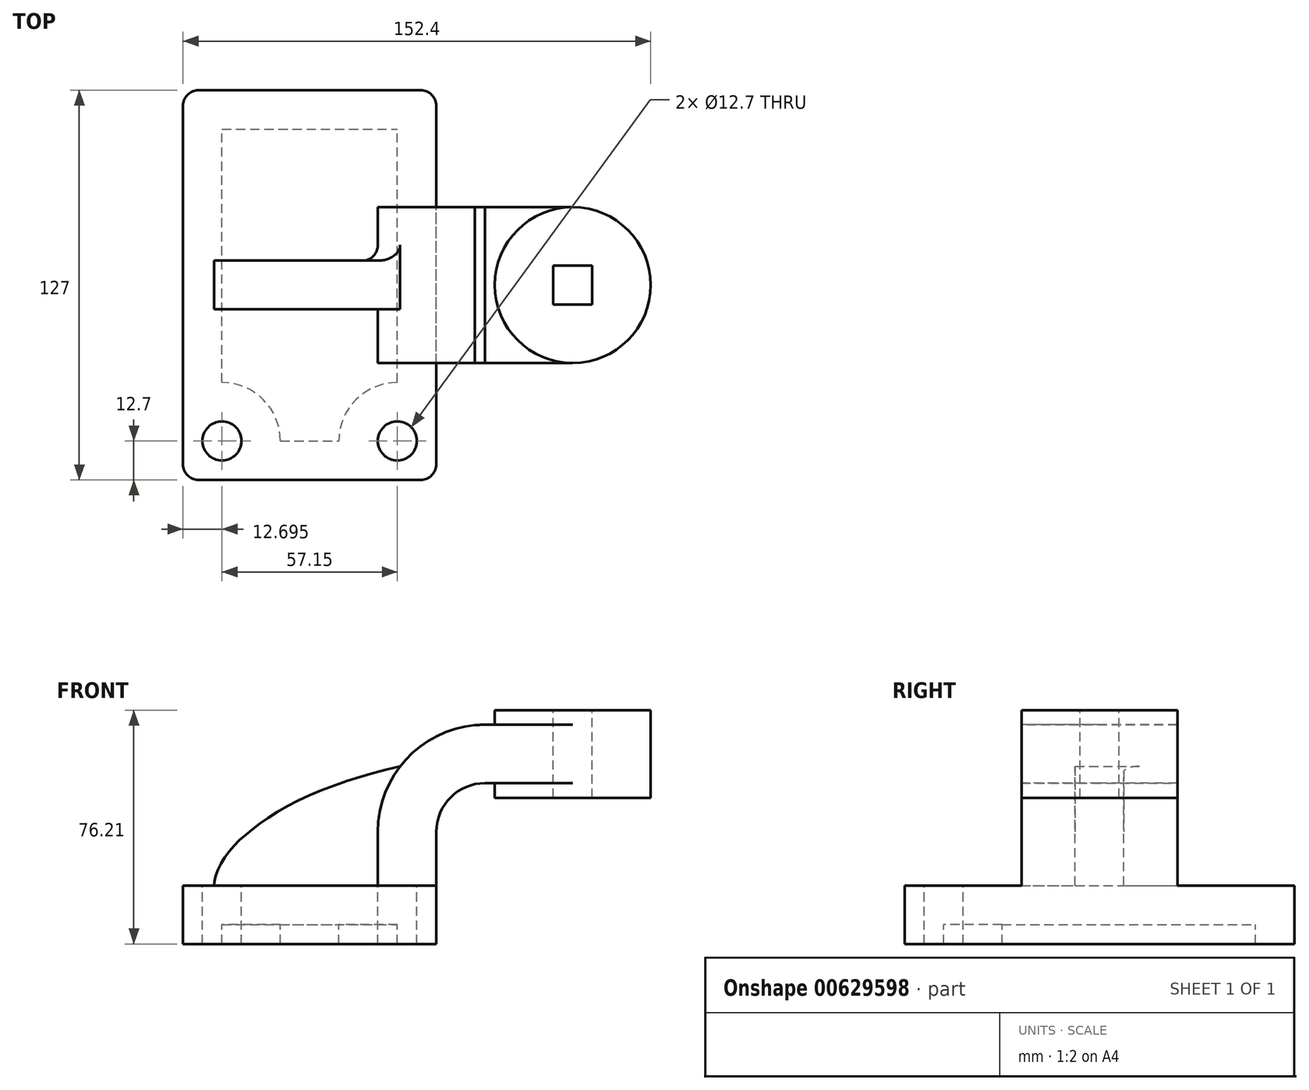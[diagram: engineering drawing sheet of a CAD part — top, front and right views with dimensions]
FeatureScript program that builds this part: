
annotation { "Feature Type Name" : "Feature", "Feature Type Description" : "" }
export const myFeature = defineFeature(function(context is Context, id is Id, definition is map)
    precondition{}
    {
        {
            var Q0;
            Q0=qCreatedBy(makeId("Front.planeOp"),FACE);
            var sketch = newSketch(context, id + "F0", { "sketchPlane" : qUnion([Q0])});
            skLineSegment(sketch, "E0.rect.bottom", {"start": v(-41.28, 9.52) * mm, "end": v(41.28, 9.52) * mm});
            skLineSegment(sketch, "E0.rect.top", {"start": v(-41.28, -9.52) * mm, "end": v(41.28, -9.52) * mm});
            skLineSegment(sketch, "E0.rect.left", {"start": v(-41.28, 9.52) * mm, "end": v(-41.28, -9.52) * mm});
            skLineSegment(sketch, "E0.rect.right", {"start": v(41.28, 9.52) * mm, "end": v(41.28, -9.52) * mm});
            skPoint(sketch, "E0.rect.middle", {"position": v(0, 0) * mm});
            skLineSegment(sketch, "E1", {"start": v(41.28, 9.52) * mm, "end": v(41.28, 27) * mm});
            skArc(sketch, "E2", {"start": v(41.28, 27) * mm, "mid": v(45.92, 38.23) * mm, "end": v(57.15, 42.88) * mm});
            skLineSegment(sketch, "E3", {"start": v(57.15, 42.88) * mm, "end": v(85.72, 42.88) * mm});
            skLineSegment(sketch, "E4.rect.bottom", {"start": v(60.32, 38.1) * mm, "end": v(111.12, 38.1) * mm});
            skLineSegment(sketch, "E4.rect.top", {"start": v(60.32, 66.68) * mm, "end": v(111.12, 66.68) * mm});
            skLineSegment(sketch, "E4.rect.left", {"start": v(60.32, 38.1) * mm, "end": v(60.32, 66.68) * mm});
            skLineSegment(sketch, "E4.rect.right", {"start": v(111.13, 38.1) * mm, "end": v(111.12, 66.68) * mm});
            skPoint(sketch, "E4.rect.middle", {"position": v(85.72, 52.39) * mm});
            skLineSegment(sketch, "E5.0", {"start": v(57.15, 61.93) * mm, "end": v(85.72, 61.93) * mm});
            skArc(sketch, "E5.1", {"start": v(22.23, 27) * mm, "mid": v(32.45, 51.7) * mm, "end": v(57.15, 61.93) * mm});
            skLineSegment(sketch, "E5.2", {"start": v(22.23, 9.52) * mm, "end": v(22.23, 27) * mm});
            skLineSegment(sketch, "E6", {"start": v(85.72, 38.1) * mm, "end": v(85.72, 66.68) * mm});
            skFitSpline(sketch, "E7", {"points": [v(-41.28, 9.53) * mm, v(57.15, 61.93) * mm], "startDerivative": vector(5.2, 92.34) * mm, "endDerivative": vector(120.92, 4.22) * mm});
            skFitSpline(sketch, "E8.0", {"points": [v(-31.13, 8.95) * mm, v(-31.07, 10.12) * mm, v(-30.68, 12.4) * mm, v(-29.3, 15.91) * mm, v(-27.01, 19.59) * mm, v(-23.75, 23.37) * mm, v(-19.56, 27.14) * mm, v(-12.83, 32.04) * mm, v(-2.55, 37.73) * mm, v(11.83, 43.44) * mm, v(27.3, 47.83) * mm, v(42.94, 50.73) * mm, v(52.85, 51.6) * mm, v(57.5, 51.77) * mm]});
            skLineSegment(sketch, "E9.0", {"start": v(-21.14, 19.69) * mm, "end": v(9.52, 19.69) * mm});
            skLineSegment(sketch, "E10.0", {"start": v(12.06, 22.23) * mm, "end": v(12.06, 27) * mm});
            skArc(sketch, "E11.0", {"start": v(12.07, 27) * mm, "mid": v(12.52, 33.38) * mm, "end": v(13.87, 39.62) * mm});
            skArc(sketch, "E12.filletArc", {"start": v(-22.9, 24.05) * mm, "mid": v(-23.5, 21.27) * mm, "end": v(-21.14, 19.69) * mm});
            skArc(sketch, "E13.filletArc", {"start": v(9.52, 19.69) * mm, "mid": v(11.32, 20.43) * mm, "end": v(12.06, 22.23) * mm});
            skArc(sketch, "E14.filletArc", {"start": v(13.87, 39.62) * mm, "mid": v(13.18, 42.18) * mm, "end": v(10.6, 42.73) * mm});
            skSolve(sketch);
        }
        {
            var Q0;
            Q0=makeQuery(id+"F0.imprint","IMPRINT",FACE,{"disambiguationData":[TD([[makeQuery(id+"F0.imprint","IMPRINT",EDGE,{"derivedFrom":sQuery(id+"F0.wireOp",EDGE,"E0.rect.top")}),1.0]])]});
            extrude(context, id + "F1", {"entities" : qUnion([Q0]), "endBound" : BoundingType.SYMMETRIC, "depth" : 127 * mm});
        }
        {
            var Q0;
            {var subQ9=sQuery(id+"F0.wireOp",EDGE,"E1");Q0=makeQuery(id+"F0.imprint","IMPRINT",FACE,{"disambiguationData":[TD([[makeQuery(id+"F0.imprint","IMPRINT",EDGE,{"derivedFrom":subQ9}),1.0]])]});}
            var Q1;
            {var subQ0=sQuery(id+"F0.wireOp",EDGE,"E6");var subQ1=sQuery(id+"F0.wireOp",EDGE,"E3");var subQ2=makeQuery(id+"F0.imprint","INTERSECT",VERTEX,{"derivedFrom":[subQ1,subQ0]});Q1=makeQuery(id+"F0.imprint","IMPRINT",FACE,{"disambiguationData":[TD([[makeQuery(id+"F0.imprint","IMPRINT",EDGE,{"disambiguationData":[TD([[subQ2,1.0]])],"derivedFrom":subQ1}),1.0]])]});}
            extrude(context, id + "F2", {"entities" : qUnion([Q0, Q1]), "operationType" : NewBodyOperationType.ADD, "endBound" : BoundingType.SYMMETRIC, "depth" : 50.8 * mm});
        }
        {
            var Q0;
            {var subQ3=sQuery(id+"F0.wireOp",EDGE,"E5.2");Q0=makeQuery(id+"F0.imprint","IMPRINT",FACE,{"disambiguationData":[TD([[makeQuery(id+"F0.imprint","IMPRINT",EDGE,{"derivedFrom":subQ3}),1.0]])]});}
            extrude(context, id + "F3", {"entities" : qUnion([Q0]), "operationType" : NewBodyOperationType.ADD, "endBound" : BoundingType.SYMMETRIC, "depth" : 15.88 * mm});
        }
        {
            var Q0;
            {var subQ5=sQuery(id+"F0.wireOp",EDGE,"E4.rect.right");Q0=makeQuery(id+"F0.imprint","IMPRINT",FACE,{"disambiguationData":[TD([[makeQuery(id+"F0.imprint","IMPRINT",EDGE,{"derivedFrom":subQ5}),1.0]])]});}
            var Q1;
            Q1=sQuery(id+"F0.wireOp",EDGE,"E6");
            revolve(context, id + "F4", {"operationType" : NewBodyOperationType.ADD, "entities" : qUnion([Q0]), "axis" : qUnion([Q1]), "revolveType" : RevolveType.FULL});
        }
        {
            var Q0;
            Q0=makeQuery(id+"F1.opExtrude","CAP_EDGE",EDGE,{"disambiguationData":[OSD([sQuery(id+"F0.wireOp",EDGE,"E0.rect.right")])],"isStart":false});
            var Q1;
            Q1=makeQuery(id+"F1.opExtrude","CAP_EDGE",EDGE,{"disambiguationData":[OSD([sQuery(id+"F0.wireOp",EDGE,"E0.rect.left")])],"isStart":false});
            var Q2;
            Q2=makeQuery(id+"F1.opExtrude","CAP_EDGE",EDGE,{"disambiguationData":[OSD([sQuery(id+"F0.wireOp",EDGE,"E0.rect.right")])],"isStart":true});
            var Q3;
            Q3=makeQuery(id+"F1.opExtrude","CAP_EDGE",EDGE,{"disambiguationData":[OSD([sQuery(id+"F0.wireOp",EDGE,"E0.rect.left")])],"isStart":true});
            fillet(context, id + "F5", {"entities" : qUnion([Q0, Q1, Q2, Q3]), "radius" : 5.08 * mm, "tangentPropagation" : true, "allowEdgeOverflow" : false});
        }
        {
            var Q0;
            {var subQ4=sQuery(id+"F0.wireOp",EDGE,"E0.rect.bottom");var subQ5=sQuery(id+"F0.wireOp",EDGE,"E0.rect.right");var subQ6=sQuery(id+"F0.wireOp",EDGE,"E0.rect.left");Q0=makeQuery(id+"F3.boolean.opBoolean","SPLIT",FACE,{"disambiguationData":[TD([makeQuery(id+"F1.opExtrude","CAP_FACE",FACE,{"disambiguationData":[OSD([subQ4,sQuery(id+"F0.wireOp",EDGE,"E0.rect.top"),subQ6,subQ5])],"isStart":false})])],"derivedFrom":makeQuery(id+"F1.opExtrude","SWEPT_FACE",FACE,{"disambiguationData":[OSD([subQ4])]})});}
            var sketch = newSketch(context, id + "F6", { "sketchPlane" : qUnion([Q0])});
            skCircle(sketch, "E15", {"center": v(-28.58, -50.8) * mm, "radius": 6.35 * mm});
            skCircle(sketch, "E16", {"center": v(28.58, -50.8) * mm, "radius": 6.35 * mm});
            skSolve(sketch);
        }
        {
            var Q0;
            Q0=makeQuery(id+"F6.imprint","IMPRINT",FACE,{"disambiguationData":[TD([[makeQuery(id+"F6.imprint","IMPRINT",EDGE,{"derivedFrom":sQuery(id+"F6.wireOp",EDGE,"E15")}),1.0]])]});
            var Q1;
            Q1=makeQuery(id+"F6.imprint","IMPRINT",FACE,{"disambiguationData":[TD([[makeQuery(id+"F6.imprint","IMPRINT",EDGE,{"derivedFrom":sQuery(id+"F6.wireOp",EDGE,"E16")}),1.0]])]});
            var Q2;
            Q2=sQuery(id+"F6.wireOp",EDGE,"E15");
            var Q3;
            Q3=sQuery(id+"F6.wireOp",EDGE,"E16");
            extrude(context, id + "F7", {"entities" : qUnion([Q0, Q1]), "operationType" : NewBodyOperationType.REMOVE, "surfaceEntities" : qUnion([Q2, Q3]), "endBound" : BoundingType.THROUGH_ALL, "oppositeDirection" : true, "depth" : 25.4 * mm, "offsetDistance" : 25.4 * mm});
        }
        {
            var Q0;
            Q0=makeQuery(id+"F4.opRevolve","SWEPT_FACE",FACE,{"disambiguationData":[OSD([sQuery(id+"F0.wireOp",EDGE,"E4.rect.top")])]});
            var sketch = newSketch(context, id + "F8", { "sketchPlane" : qUnion([Q0])});
            skLineSegment(sketch, "E17.bottom", {"start": v(92.08, 6.35) * mm, "end": v(79.38, 6.35) * mm});
            skLineSegment(sketch, "E17.top", {"start": v(92.08, -6.35) * mm, "end": v(79.38, -6.35) * mm});
            skLineSegment(sketch, "E17.left", {"start": v(92.08, 6.35) * mm, "end": v(92.08, -6.35) * mm});
            skLineSegment(sketch, "E17.right", {"start": v(79.38, 6.35) * mm, "end": v(79.38, -6.35) * mm});
            skLineSegment(sketch, "E18", {"start": v(85.73, 6.35) * mm, "end": v(85.73, -6.35) * mm});
            skSolve(sketch);
        }
        {
            var Q0;
            Q0 = qSketchRegion(id + "F8", true);
            extrude(context, id + "F9", {"entities" : qUnion([Q0]), "operationType" : NewBodyOperationType.REMOVE, "endBound" : BoundingType.THROUGH_ALL, "oppositeDirection" : true, "depth" : 25.4 * mm, "offsetDistance" : 25.4 * mm});
        }
        {
            var Q0;
            Q0=makeQuery(id+"F1.opExtrude","SWEPT_FACE",FACE,{"disambiguationData":[OSD([sQuery(id+"F0.wireOp",EDGE,"E0.rect.top")])]});
            shell(context, id + "F10", {"entities" : qUnion([Q0]), "thickness" : 12.7 * mm});
        }
        {
            var Q0;
            Q0=makeQuery(id+"F3.opExtrude","CAP_EDGE",EDGE,{"disambiguationData":[OSD([sQuery(id+"F0.wireOp",EDGE,"E0.rect.bottom")])],"isStart":false});
            var Q1;
            {var subQ0=sQuery(id+"F0.wireOp",EDGE,"E0.rect.bottom");var subQ1=sQuery(id+"F0.wireOp",EDGE,"E7");var subQ2=sQuery(id+"F0.wireOp",EDGE,"E5.2");var subQ3=sQuery(id+"F0.wireOp",EDGE,"E5.1");Q1=makeQuery(id+"F3.boolean.opBoolean","SPLIT",EDGE,{"disambiguationData":[TD([makeQuery(id+"F2.opExtrude","CAP_FACE",FACE,{"disambiguationData":[OSD([subQ0,sQuery(id+"F0.wireOp",EDGE,"E1"),sQuery(id+"F0.wireOp",EDGE,"E2"),sQuery(id+"F0.wireOp",EDGE,"E3"),sQuery(id+"F0.wireOp",EDGE,"E5.0"),subQ3,subQ2,sQuery(id+"F0.wireOp",EDGE,"E6"),subQ1])],"isStart":false})])],"derivedFrom":makeQuery(id+"F2.opExtrude","SWEPT_EDGE",EDGE,{"disambiguationData":[OSD([subQ0,subQ2])]})});}
            var Q2;
            Q2=makeQuery(id+"F2.opExtrude","CAP_EDGE",EDGE,{"disambiguationData":[OSD([sQuery(id+"F0.wireOp",EDGE,"E0.rect.bottom")])],"isStart":false});
            var Q3;
            Q3=makeQuery(id+"F3.opExtrude","CAP_EDGE",EDGE,{"disambiguationData":[OSD([sQuery(id+"F0.wireOp",EDGE,"E5.2")])],"isStart":false});
            var Q4;
            Q4=makeQuery(id+"F3.opExtrude","CAP_EDGE",EDGE,{"disambiguationData":[OSD([sQuery(id+"F0.wireOp",EDGE,"E0.rect.bottom")])],"isStart":true});
            var Q5;
            {var subQ0=sQuery(id+"F0.wireOp",EDGE,"E0.rect.bottom");var subQ1=sQuery(id+"F0.wireOp",EDGE,"E7");var subQ2=sQuery(id+"F0.wireOp",EDGE,"E5.2");var subQ3=sQuery(id+"F0.wireOp",EDGE,"E5.1");Q5=makeQuery(id+"F3.boolean.opBoolean","SPLIT",EDGE,{"disambiguationData":[TD([makeQuery(id+"F2.opExtrude","CAP_FACE",FACE,{"disambiguationData":[OSD([subQ0,sQuery(id+"F0.wireOp",EDGE,"E1"),sQuery(id+"F0.wireOp",EDGE,"E2"),sQuery(id+"F0.wireOp",EDGE,"E3"),sQuery(id+"F0.wireOp",EDGE,"E5.0"),subQ3,subQ2,sQuery(id+"F0.wireOp",EDGE,"E6"),subQ1])],"isStart":true})])],"derivedFrom":makeQuery(id+"F2.opExtrude","SWEPT_EDGE",EDGE,{"disambiguationData":[OSD([subQ0,subQ2])]})});}
            var Q6;
            Q6=makeQuery(id+"F2.opExtrude","CAP_EDGE",EDGE,{"disambiguationData":[OSD([sQuery(id+"F0.wireOp",EDGE,"E0.rect.bottom")])],"isStart":true});
            var Q7;
            Q7=makeQuery(id+"F3.opExtrude","CAP_EDGE",EDGE,{"disambiguationData":[OSD([sQuery(id+"F0.wireOp",EDGE,"E5.2")])],"isStart":true});
            fillet(context, id + "F11", {"entities" : qUnion([Q0, Q1, Q2, Q3, Q4, Q5, Q6, Q7]), "radius" : 5.08 * mm, "tangentPropagation" : true, "allowEdgeOverflow" : false});
        }
    });
